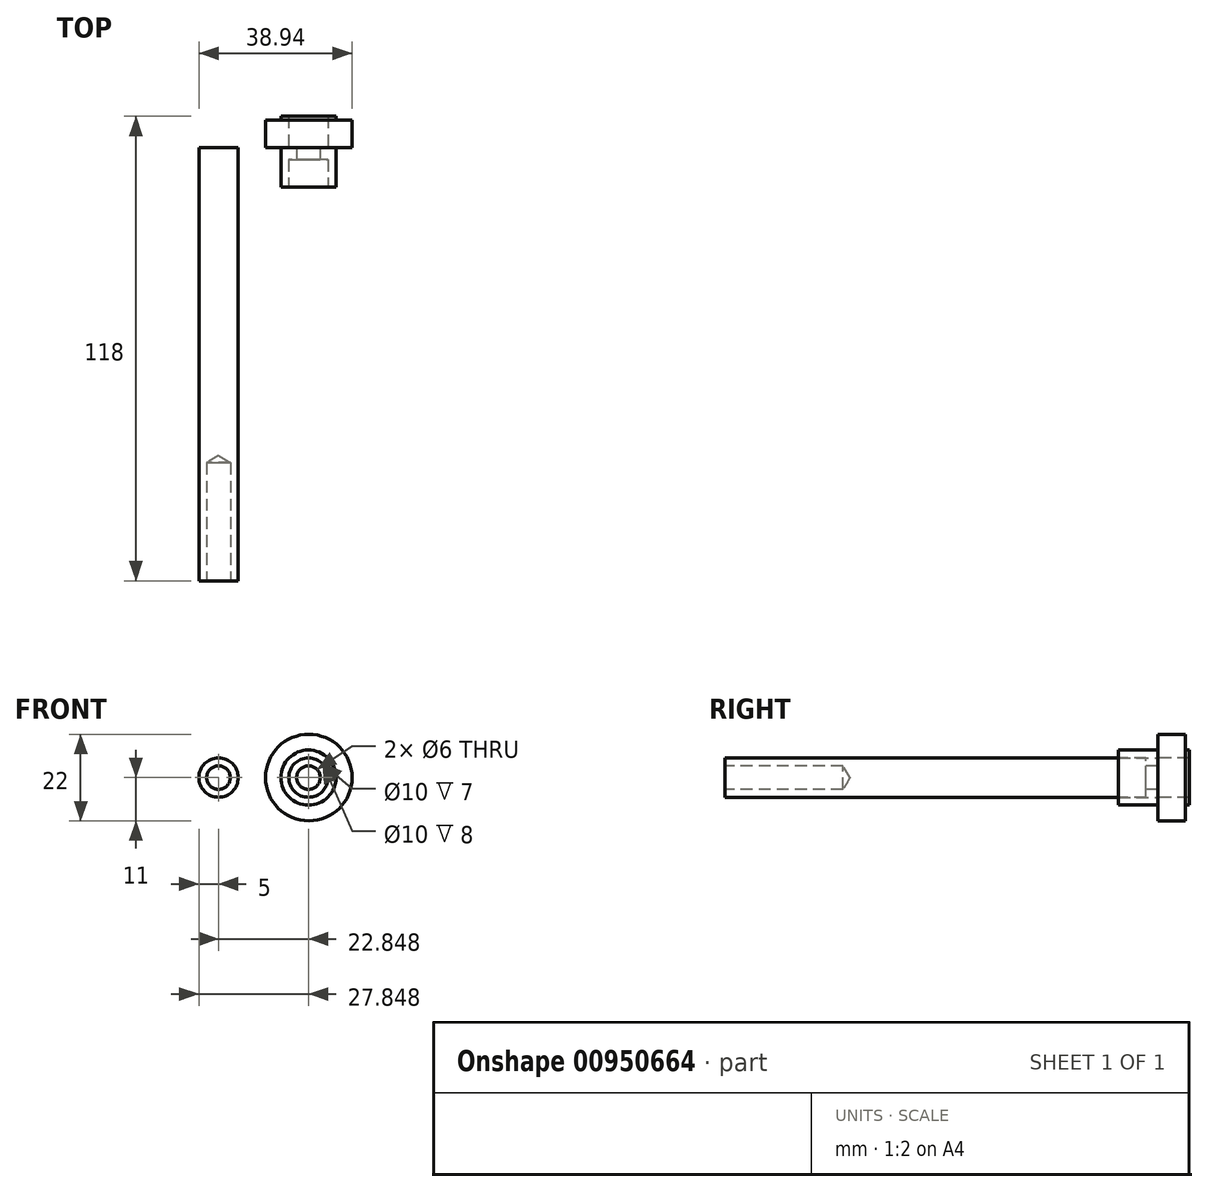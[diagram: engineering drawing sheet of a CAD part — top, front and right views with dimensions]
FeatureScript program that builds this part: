
annotation { "Feature Type Name" : "Feature", "Feature Type Description" : "" }
export const myFeature = defineFeature(function(context is Context, id is Id, definition is map)
    precondition{}
    {
        {
            var Q0;
            Q0=qCreatedBy(makeId("Front.planeOp"),FACE);
            var sketch = newSketch(context, id + "F0", { "sketchPlane" : qUnion([Q0])});
            skCircle(sketch, "E0", {"center": v(0, 0) * mm, "radius": 5 * mm});
            skSolve(sketch);
        }
        {
            var Q0;
            Q0=makeQuery(id+"F0.imprint","IMPRINT",FACE,{"disambiguationData":[TD([[makeQuery(id+"F0.imprint","IMPRINT",EDGE,{"derivedFrom":sQuery(id+"F0.wireOp",EDGE,"E0")}),1.0]])]});
            extrude(context, id + "F1", {"entities" : qUnion([Q0]), "depth" : 110 * mm, "offsetDistance" : 25 * mm});
        }
        {
            var Q0;
            Q0=makeQuery(id+"F1.opExtrude","CAP_FACE",FACE,{"disambiguationData":[OSD([sQuery(id+"F0.wireOp",EDGE,"E0")])],"isStart":false});
            var sketch = newSketch(context, id + "F2", { "sketchPlane" : qUnion([Q0])});
            skPoint(sketch, "E1", {"position": v(0, 0) * mm});
            skSolve(sketch);
        }
        {
            var Q0;
            Q0=sQuery(id+"F2.wireOp",VERTEX,"E1");
            var Q1;
            Q1=makeQuery(id+"F1.opExtrude","SWEPT_BODY",BODY,{"disambiguationData":[OSD([sQuery(id+"F0.wireOp",EDGE,"E0")])]});
            hole(context, id + "F3", {"style" : HoleStyle.SIMPLE, "endStyle" : HoleEndStyle.BLIND, "holeDiameter" : 6 * mm, "majorDiameter" : 5 * mm, "holeDepth" : 30 * mm, "isTappedThrough" : true, "tappedDepth" : 12 * mm, "tapClearance" : 3, "locations" : qUnion([Q0]), "scope" : qUnion([Q1])});
        }
        {
            var Q0;
            Q0=qCreatedBy(makeId("Front.planeOp"),FACE);
            var sketch = newSketch(context, id + "F4", { "sketchPlane" : qUnion([Q0])});
            skCircle(sketch, "E2", {"center": v(22.85, 0) * mm, "radius": 7 * mm});
            skSolve(sketch);
        }
        {
            var Q0;
            Q0=makeQuery(id+"F4.imprint","IMPRINT",FACE,{"disambiguationData":[TD([[makeQuery(id+"F4.imprint","IMPRINT",EDGE,{"derivedFrom":sQuery(id+"F4.wireOp",EDGE,"E2")}),1.0]])]});
            extrude(context, id + "F5", {"entities" : qUnion([Q0]), "depth" : 10 * mm, "offsetDistance" : 25 * mm});
        }
        {
            var Q0;
            Q0=makeQuery(id+"F5.opExtrude","CAP_FACE",FACE,{"disambiguationData":[OSD([sQuery(id+"F4.wireOp",EDGE,"E2")])],"isStart":false});
            var sketch = newSketch(context, id + "F6", { "sketchPlane" : qUnion([Q0])});
            skPoint(sketch, "E3", {"position": v(22.85, 0) * mm});
            skSolve(sketch);
        }
        {
            var Q0;
            Q0=sQuery(id+"F6.wireOp",VERTEX,"E3");
            var Q1;
            Q1=makeQuery(id+"F5.opExtrude","SWEPT_BODY",BODY,{"disambiguationData":[OSD([sQuery(id+"F4.wireOp",EDGE,"E2")])]});
            hole(context, id + "F7", {"style" : HoleStyle.C_BORE, "endStyle" : HoleEndStyle.BLIND, "holeDiameter" : 6 * mm, "cBoreDiameter" : 10 * mm, "cBoreDepth" : 7 * mm, "majorDiameter" : 5 * mm, "holeDepth" : 10 * mm, "isTappedThrough" : true, "tappedDepth" : 12 * mm, "tapClearance" : 3, "locations" : qUnion([Q0]), "scope" : qUnion([Q1])});
        }
        {
            var Q0;
            Q0=makeQuery(id+"F5.opExtrude","CAP_FACE",FACE,{"disambiguationData":[OSD([sQuery(id+"F4.wireOp",EDGE,"E2")])],"isStart":true});
            var sketch = newSketch(context, id + "F8", { "sketchPlane" : qUnion([Q0])});
            skCircle(sketch, "E4", {"center": v(-22.85, 0) * mm, "radius": 7 * mm});
            skCircle(sketch, "E5", {"center": v(-22.85, 0) * mm, "radius": 5 * mm});
            skSolve(sketch);
        }
        {
            var Q0;
            Q0=makeQuery(id+"F8.imprint","IMPRINT",FACE,{"disambiguationData":[TD([[makeQuery(id+"F8.imprint","IMPRINT",EDGE,{"derivedFrom":sQuery(id+"F8.wireOp",EDGE,"E4")}),-1.0]])]});
            extrude(context, id + "F9", {"entities" : qUnion([Q0]), "operationType" : NewBodyOperationType.ADD, "depth" : 8 * mm, "offsetDistance" : 25 * mm});
        }
        {
            var Q0;
            Q0=qCreatedBy(makeId("Front.planeOp"),FACE);
            var sketch = newSketch(context, id + "F10", { "sketchPlane" : qUnion([Q0])});
            skCircle(sketch, "E6", {"center": v(22.94, 0) * mm, "radius": 11 * mm});
            skSolve(sketch);
        }
        {
            var Q0;
            Q0=makeQuery(id+"F10.imprint","IMPRINT",FACE,{"disambiguationData":[TD([[makeQuery(id+"F10.imprint","IMPRINT",EDGE,{"derivedFrom":sQuery(id+"F10.wireOp",EDGE,"E6")}),1.0]])]});
            extrude(context, id + "F11", {"entities" : qUnion([Q0]), "operationType" : NewBodyOperationType.ADD, "oppositeDirection" : true, "depth" : 7 * mm, "offsetDistance" : 25 * mm});
        }
        {
            var Q0;
            Q0=makeQuery(id+"F11.boolean.opBoolean","SPLIT",FACE,{"disambiguationData":[TD([makeQuery(id+"F9.opExtrude","SWEPT_FACE",FACE,{"disambiguationData":[OSD([sQuery(id+"F8.wireOp",EDGE,"E5")])]})])],"derivedFrom":makeQuery(id+"F11.opExtrude","CAP_FACE",FACE,{"disambiguationData":[OSD([sQuery(id+"F10.wireOp",EDGE,"E6")])],"isStart":false})});
            extrude(context, id + "F12", {"entities" : qUnion([Q0]), "operationType" : NewBodyOperationType.REMOVE, "oppositeDirection" : true, "depth" : 7 * mm, "offsetDistance" : 25 * mm});
        }
    });
